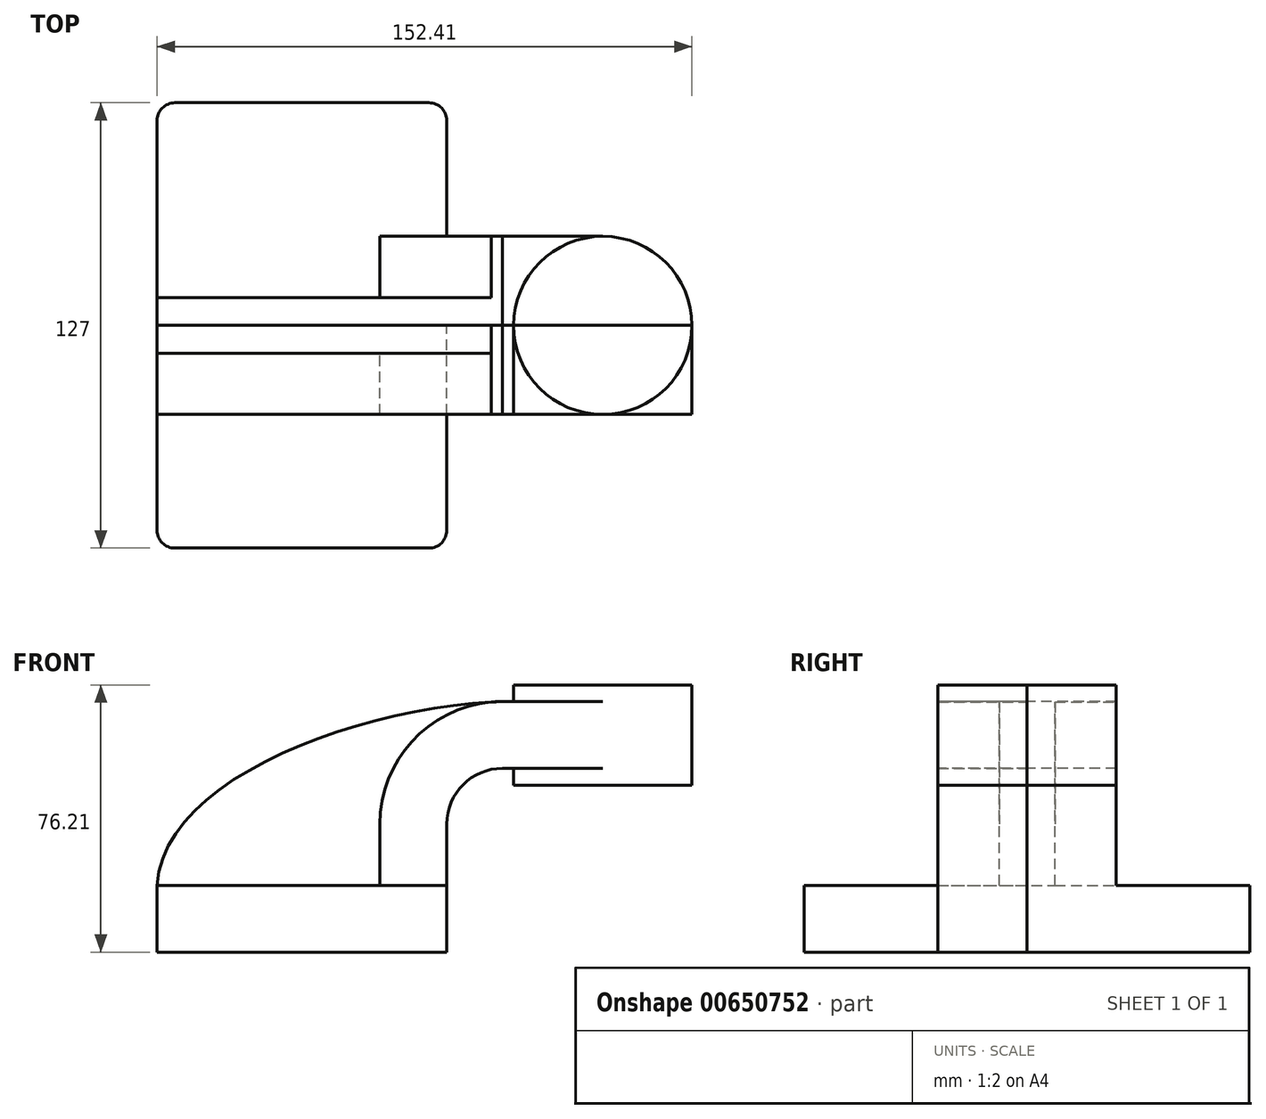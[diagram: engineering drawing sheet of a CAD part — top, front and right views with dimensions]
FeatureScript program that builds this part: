
annotation { "Feature Type Name" : "Feature", "Feature Type Description" : "" }
export const myFeature = defineFeature(function(context is Context, id is Id, definition is map)
    precondition{}
    {
        {
            var Q0;
            Q0=qCreatedBy(makeId("Front.planeOp"),FACE);
            var sketch = newSketch(context, id + "F0", { "sketchPlane" : qUnion([Q0])});
            skLineSegment(sketch, "E0.rect.bottom", {"start": v(-41.28, 9.52) * mm, "end": v(41.28, 9.52) * mm});
            skLineSegment(sketch, "E0.rect.top", {"start": v(-41.28, -9.52) * mm, "end": v(41.28, -9.52) * mm});
            skLineSegment(sketch, "E0.rect.left", {"start": v(-41.28, 9.52) * mm, "end": v(-41.28, -9.52) * mm});
            skLineSegment(sketch, "E0.rect.right", {"start": v(41.28, 9.52) * mm, "end": v(41.28, -9.52) * mm});
            skPoint(sketch, "E0.rect.middle", {"position": v(0, 0) * mm});
            skLineSegment(sketch, "E1", {"start": v(41.28, 9.52) * mm, "end": v(41.28, 27) * mm});
            skArc(sketch, "E2", {"start": v(41.28, 27) * mm, "mid": v(45.92, 38.23) * mm, "end": v(57.15, 42.88) * mm});
            skLineSegment(sketch, "E3", {"start": v(57.15, 42.88) * mm, "end": v(85.72, 42.88) * mm});
            skLineSegment(sketch, "E4.rect.bottom", {"start": v(60.32, 38.1) * mm, "end": v(111.12, 38.1) * mm});
            skLineSegment(sketch, "E4.rect.top", {"start": v(60.32, 66.68) * mm, "end": v(111.12, 66.68) * mm});
            skLineSegment(sketch, "E4.rect.left", {"start": v(60.32, 38.1) * mm, "end": v(60.32, 66.68) * mm});
            skLineSegment(sketch, "E4.rect.right", {"start": v(111.13, 38.1) * mm, "end": v(111.12, 66.68) * mm});
            skPoint(sketch, "E4.rect.middle", {"position": v(85.72, 52.39) * mm});
            skLineSegment(sketch, "E5.0", {"start": v(57.15, 61.93) * mm, "end": v(85.72, 61.93) * mm});
            skArc(sketch, "E5.1", {"start": v(22.23, 27) * mm, "mid": v(32.45, 51.7) * mm, "end": v(57.15, 61.93) * mm});
            skLineSegment(sketch, "E5.2", {"start": v(22.23, 9.52) * mm, "end": v(22.23, 27) * mm});
            skLineSegment(sketch, "E6", {"start": v(85.72, 38.1) * mm, "end": v(85.72, 66.68) * mm});
            skFitSpline(sketch, "E7", {"points": [v(-41.28, 9.53) * mm, v(57.15, 61.93) * mm], "startDerivative": vector(5.2, 92.34) * mm, "endDerivative": vector(120.92, 4.22) * mm});
            skSolve(sketch);
        }
        {
            var Q0;
            Q0=makeQuery(id+"F0.imprint","IMPRINT",FACE,{"disambiguationData":[TD([[makeQuery(id+"F0.imprint","IMPRINT",EDGE,{"derivedFrom":sQuery(id+"F0.wireOp",EDGE,"E0.rect.top")}),1.0]])]});
            extrude(context, id + "F1", {"entities" : qUnion([Q0]), "endBound" : BoundingType.SYMMETRIC, "depth" : 127 * mm});
        }
        {
            var Q0;
            {var subQ9=sQuery(id+"F0.wireOp",EDGE,"E1");Q0=makeQuery(id+"F0.imprint","IMPRINT",FACE,{"disambiguationData":[TD([[makeQuery(id+"F0.imprint","IMPRINT",EDGE,{"derivedFrom":subQ9}),1.0]])]});}
            var Q1;
            {var subQ0=sQuery(id+"F0.wireOp",EDGE,"E6");var subQ1=sQuery(id+"F0.wireOp",EDGE,"E3");var subQ2=makeQuery(id+"F0.imprint","INTERSECT",VERTEX,{"derivedFrom":[subQ1,subQ0]});Q1=makeQuery(id+"F0.imprint","IMPRINT",FACE,{"disambiguationData":[TD([[makeQuery(id+"F0.imprint","IMPRINT",EDGE,{"disambiguationData":[TD([[subQ2,1.0]])],"derivedFrom":subQ1}),1.0]])]});}
            extrude(context, id + "F2", {"entities" : qUnion([Q0, Q1]), "operationType" : NewBodyOperationType.ADD, "endBound" : BoundingType.SYMMETRIC, "depth" : 50.8 * mm});
        }
        {
            var Q0;
            {var subQ3=sQuery(id+"F0.wireOp",EDGE,"E5.2");Q0=makeQuery(id+"F0.imprint","IMPRINT",FACE,{"disambiguationData":[TD([[makeQuery(id+"F0.imprint","IMPRINT",EDGE,{"derivedFrom":subQ3}),1.0]])]});}
            extrude(context, id + "F3", {"entities" : qUnion([Q0]), "operationType" : NewBodyOperationType.ADD, "endBound" : BoundingType.SYMMETRIC, "depth" : 15.88 * mm});
        }
        {
            var Q0;
            {var subQ5=sQuery(id+"F0.wireOp",EDGE,"E4.rect.right");Q0=makeQuery(id+"F0.imprint","IMPRINT",FACE,{"disambiguationData":[TD([[makeQuery(id+"F0.imprint","IMPRINT",EDGE,{"derivedFrom":subQ5}),1.0]])]});}
            var Q1;
            Q1=sQuery(id+"F0.wireOp",EDGE,"E6");
            revolve(context, id + "F4", {"operationType" : NewBodyOperationType.ADD, "entities" : qUnion([Q0]), "axis" : qUnion([Q1]), "revolveType" : RevolveType.FULL});
        }
        {
            var Q0;
            Q0=makeQuery(id+"F1.opExtrude","CAP_EDGE",EDGE,{"disambiguationData":[OSD([sQuery(id+"F0.wireOp",EDGE,"E0.rect.right")])],"isStart":false});
            var Q1;
            Q1=makeQuery(id+"F1.opExtrude","CAP_EDGE",EDGE,{"disambiguationData":[OSD([sQuery(id+"F0.wireOp",EDGE,"E0.rect.left")])],"isStart":false});
            var Q2;
            Q2=makeQuery(id+"F1.opExtrude","CAP_EDGE",EDGE,{"disambiguationData":[OSD([sQuery(id+"F0.wireOp",EDGE,"E0.rect.right")])],"isStart":true});
            var Q3;
            Q3=makeQuery(id+"F1.opExtrude","CAP_EDGE",EDGE,{"disambiguationData":[OSD([sQuery(id+"F0.wireOp",EDGE,"E0.rect.left")])],"isStart":true});
            fillet(context, id + "F5", {"entities" : qUnion([Q0, Q1, Q2, Q3]), "radius" : 5.08 * mm, "tangentPropagation" : true, "allowEdgeOverflow" : false});
        }
        {
            var Q0;
            Q0 = qSketchRegion(id + "F0", true);
            extrude(context, id + "F6", {"entities" : qUnion([Q0]), "depth" : 25.4 * mm, "offsetDistance" : 25.4 * mm});
        }
    });
